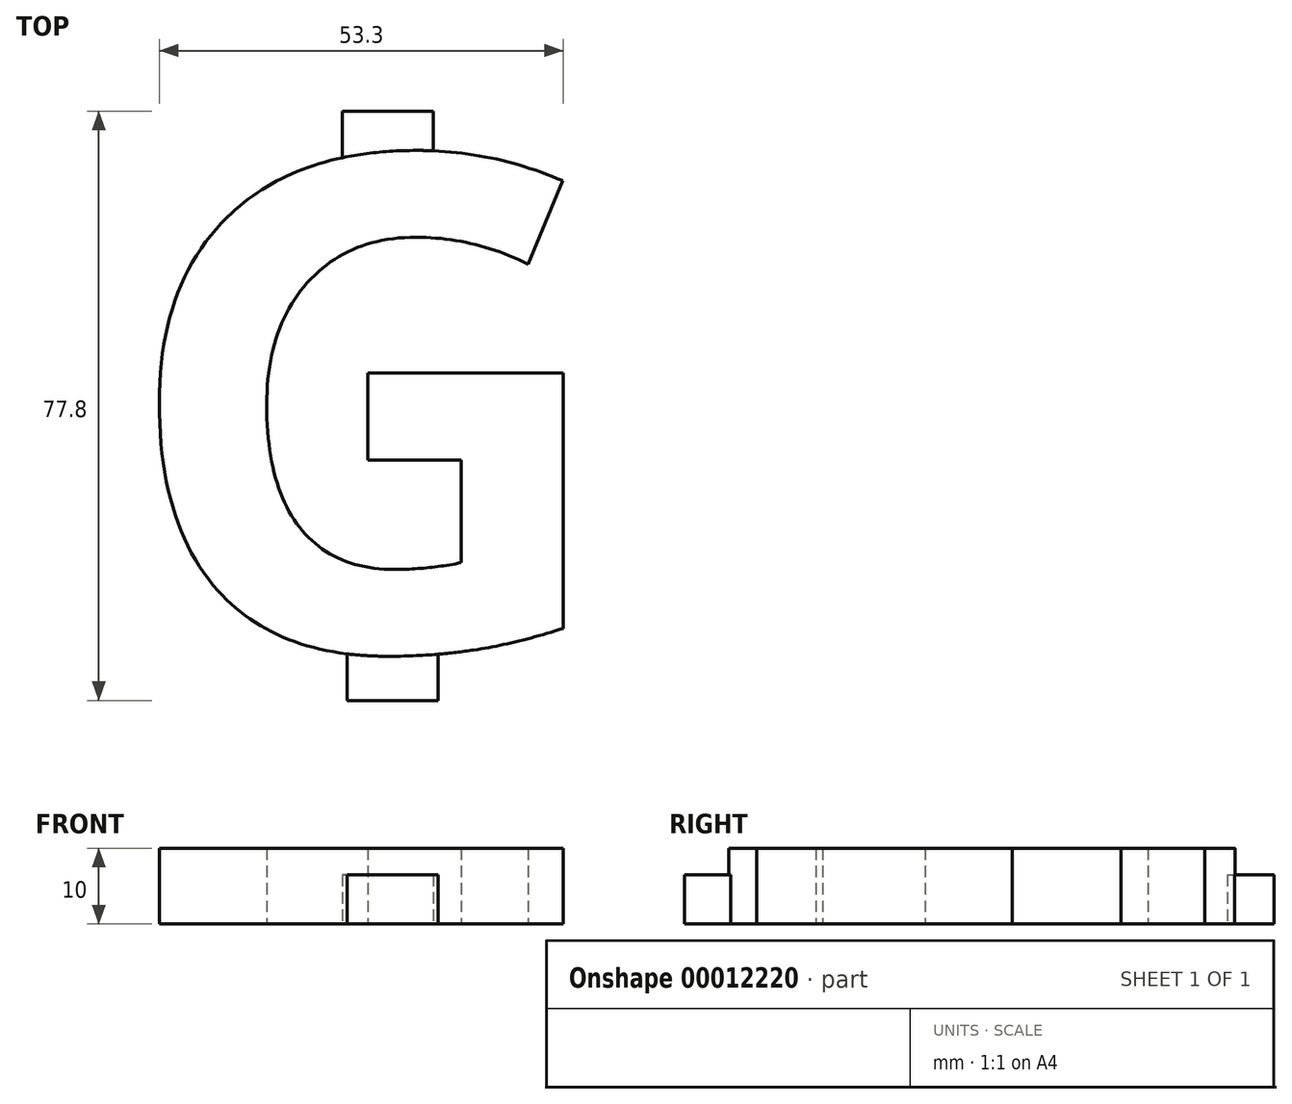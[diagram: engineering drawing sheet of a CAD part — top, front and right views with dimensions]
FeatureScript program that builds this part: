
annotation { "Feature Type Name" : "Feature", "Feature Type Description" : "" }
export const myFeature = defineFeature(function(context is Context, id is Id, definition is map)
    precondition{}
    {
        {
            var Q0;
            Q0=qCreatedBy(makeId("Top.planeOp"),FACE);
            var sketch = newSketch(context, id + "F0", { "sketchPlane" : qUnion([Q0])});
            skText(sketch, "E0", { "text": "G", "fontName": "OpenSans-Bold.ttf"});
            skLineSegment(sketch, "E1.rect.bottom", {"start": v(-16.54, -6.74) * mm, "end": v(-28.54, -6.74) * mm});
            skLineSegment(sketch, "E1.rect.top", {"start": v(-16.54, -0.34) * mm, "end": v(-28.54, -0.34) * mm});
            skLineSegment(sketch, "E1.rect.left", {"start": v(-16.54, -6.74) * mm, "end": v(-16.54, -0.34) * mm});
            skLineSegment(sketch, "E1.rect.right", {"start": v(-28.54, -6.74) * mm, "end": v(-28.54, -0.34) * mm});
            skPoint(sketch, "E1.rect.middle", {"position": v(-22.54, -3.54) * mm});
            skLineSegment(sketch, "E2", {"start": v(-33.98, -0.95) * mm, "end": v(-5.24, -0.95) * mm, "construction": true});
            skLineSegment(sketch, "E3.rect.bottom", {"start": v(-17.16, 64.56) * mm, "end": v(-29.16, 64.56) * mm});
            skLineSegment(sketch, "E3.rect.left", {"start": v(-17.16, 64.56) * mm, "end": v(-17.16, 71.06) * mm});
            skLineSegment(sketch, "E3.rect.top", {"start": v(-17.16, 71.06) * mm, "end": v(-29.16, 71.06) * mm});
            skLineSegment(sketch, "E3.rect.right", {"start": v(-29.16, 64.56) * mm, "end": v(-29.16, 71.06) * mm});
            skPoint(sketch, "E3.rect.middle", {"position": v(-23.16, 67.81) * mm});
            const initialGuessF0  = {"E0": [-0.0586, 0, 1, 0, 0.0655]};
            skSetInitialGuess(sketch, initialGuessF0);
            skSolve(sketch);
        }
        {
            var Q0;
            Q0=makeQuery(id+"F0.imprint","IMPRINT",FACE,{"disambiguationData":[TD([[makeQuery(id+"F0.imprint","IMPRINT",EDGE,{"derivedFrom":sQuery(id+"F0.wireOp",EDGE,"E0.sketch_text.stroke-0")}),-1.0]])]});
            var Q1;
            {var subQ1=sQuery(id+"F0.wireOp",EDGE,"E3.rect.bottom");Q1=makeQuery(id+"F0.imprint","IMPRINT",FACE,{"disambiguationData":[TD([[makeQuery(id+"F0.imprint","IMPRINT",EDGE,{"derivedFrom":subQ1}),-1.0]])]});}
            var Q2;
            {var subQ1=sQuery(id+"F0.wireOp",EDGE,"E1.rect.top");Q2=makeQuery(id+"F0.imprint","IMPRINT",FACE,{"disambiguationData":[TD([[makeQuery(id+"F0.imprint","IMPRINT",EDGE,{"derivedFrom":subQ1}),1.0]])]});}
            extrude(context, id + "F1", {"entities" : qUnion([Q0, Q1, Q2]), "depth" : 10 * mm});
        }
        {
            var Q0;
            {var subQ1=sQuery(id+"F0.wireOp",EDGE,"E1.rect.bottom");Q0=makeQuery(id+"F0.imprint","IMPRINT",FACE,{"disambiguationData":[TD([[makeQuery(id+"F0.imprint","IMPRINT",EDGE,{"derivedFrom":subQ1}),-1.0]])]});}
            var Q1;
            {var subQ0=sQuery(id+"F0.wireOp",EDGE,"E3.rect.top");Q1=makeQuery(id+"F0.imprint","IMPRINT",FACE,{"disambiguationData":[TD([[makeQuery(id+"F0.imprint","IMPRINT",EDGE,{"derivedFrom":subQ0}),1.0]])]});}
            extrude(context, id + "F2", {"entities" : qUnion([Q0, Q1]), "operationType" : NewBodyOperationType.ADD, "depth" : 6.5 * mm});
        }
    });
